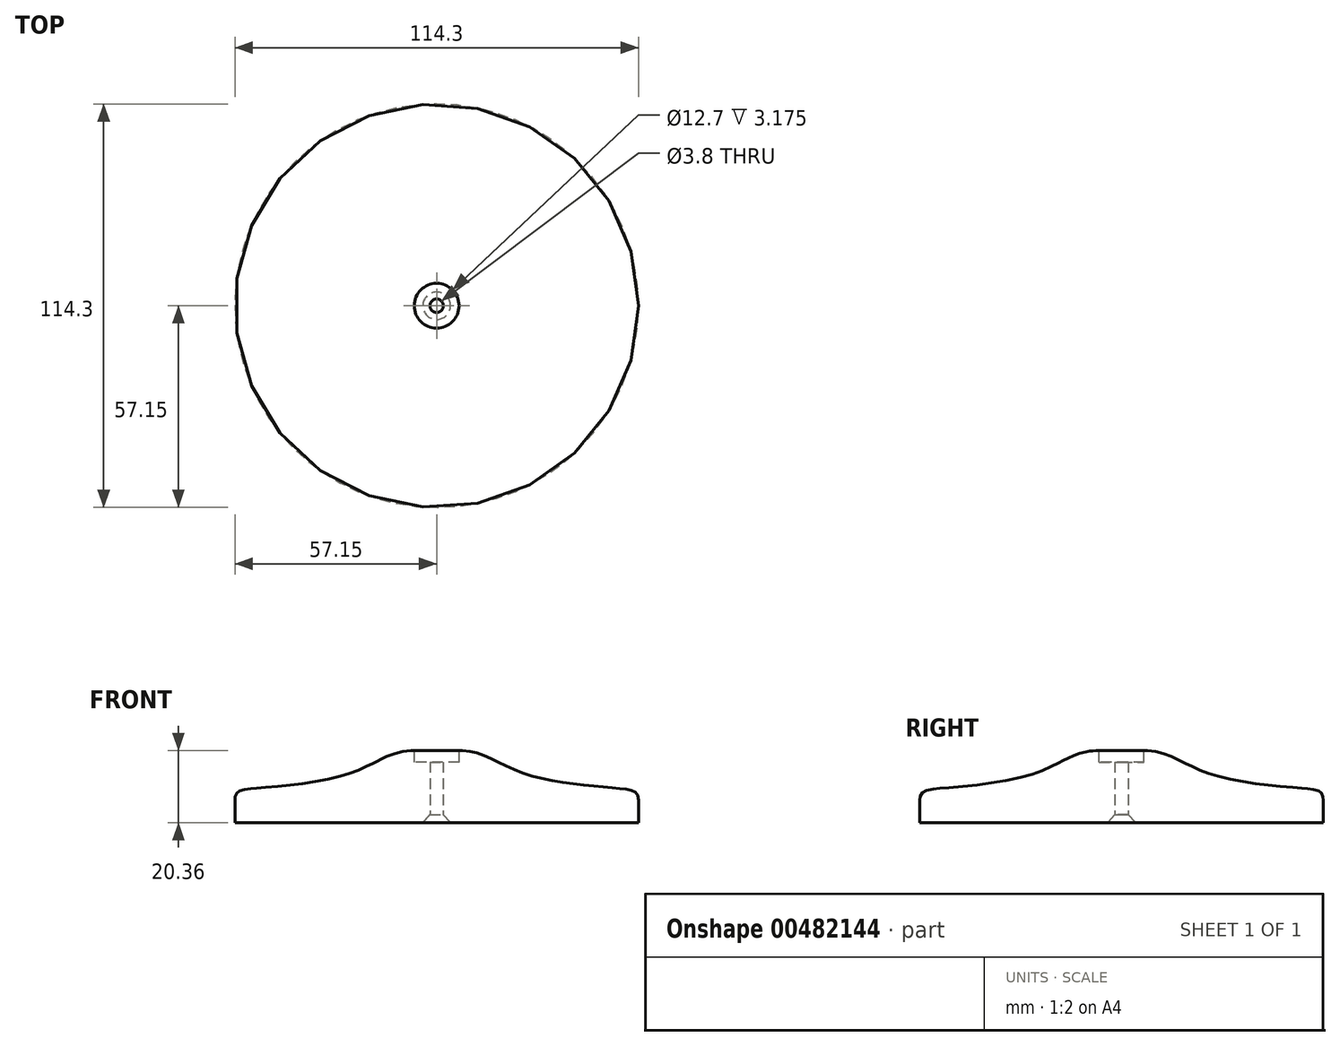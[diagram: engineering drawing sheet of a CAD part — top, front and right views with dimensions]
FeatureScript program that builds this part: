
annotation { "Feature Type Name" : "Feature", "Feature Type Description" : "" }
export const myFeature = defineFeature(function(context is Context, id is Id, definition is map)
    precondition{}
    {
        {
            var Q0;
            Q0=qCreatedBy(makeId("Top.planeOp"),FACE);
            var sketch = newSketch(context, id + "F0", { "sketchPlane" : qUnion([Q0])});
            skCircle(sketch, "E0", {"center": v(0, 0) * mm, "radius": 28.58 * mm, "construction": true});
            skSolve(sketch);
        }
        {
            var Q0;
            Q0=qCreatedBy(makeId("Front.planeOp"),FACE);
            var sketch = newSketch(context, id + "F1", { "sketchPlane" : qUnion([Q0])});
            skLineSegment(sketch, "E1", {"start": v(-57.15, 0) * mm, "end": v(0, 0) * mm});
            skLineSegment(sketch, "E2", {"start": v(-57.15, 0) * mm, "end": v(-57.15, 6.35) * mm});
            skFitSpline(sketch, "E3", {"points": [v(-57.15, 6.35) * mm, v(-52.75, 9.56) * mm, v(-24.5, 14) * mm, v(-6.35, 20.32) * mm], "startDerivative": vector(-0.27, 40.29) * mm, "endDerivative": vector(51.76, -3.83) * mm});
            skLineSegment(sketch, "E4", {"start": v(0, 0) * mm, "end": v(0, 17.15) * mm});
            skLineSegment(sketch, "E5", {"start": v(-6.35, 20.32) * mm, "end": v(-6.35, 17.15) * mm});
            skLineSegment(sketch, "E6", {"start": v(-6.35, 17.15) * mm, "end": v(0, 17.15) * mm});
            skLineSegment(sketch, "E7", {"start": v(0, 23.15) * mm, "end": v(0, -3.4) * mm, "construction": true});
            skSolve(sketch);
        }
        {
            var Q0;
            {var subQ1=sQuery(id+"F1.wireOp",EDGE,"E1");Q0=makeQuery(id+"F1.imprint","IMPRINT",FACE,{"disambiguationData":[TD([[makeQuery(id+"F1.imprint","IMPRINT",EDGE,{"derivedFrom":subQ1}),1.0]])]});}
            var Q1;
            Q1=sQuery(id+"F1.wireOp",EDGE,"E7");
            revolve(context, id + "F2", {"entities" : qUnion([Q0]), "axis" : qUnion([Q1]), "revolveType" : RevolveType.FULL});
        }
        {
            var Q0;
            Q0=sQuery(id+"F0.wireOp",VERTEX,"E0.center");
            var Q1;
            Q1=makeQuery(id+"F2.opRevolve","SWEPT_BODY",BODY,{"disambiguationData":[OSD([sQuery(id+"F1.wireOp",EDGE,"E1"),sQuery(id+"F1.wireOp",EDGE,"E2"),sQuery(id+"F1.wireOp",EDGE,"E3"),sQuery(id+"F1.wireOp",EDGE,"E4"),sQuery(id+"F1.wireOp",EDGE,"E5"),sQuery(id+"F1.wireOp",EDGE,"E6")])]});
            hole(context, id + "F3", {"style" : HoleStyle.C_SINK, "endStyle" : HoleEndStyle.THROUGH, "oppositeDirection" : true, "standardTappedOrClearance" : lookupTablePath({ "standard" : "ANSI", "fit" : "Normal (ASME)", "size" : "#6", "type" : "Clearance" }), "standardBlindInLast" : lookupTablePath({ "fit" : "Free", "standard" : "ANSI", "size" : "#6", "type" : "Clearance" }), "holeDiameter" : 3.8 * mm, "cSinkDiameter" : 7.8 * mm, "cSinkAngle" : 82 * degree, "isTappedThrough" : true, "tappedDepth" : 12.7 * mm, "tapClearance" : 3, "locations" : qUnion([Q0]), "scope" : qUnion([Q1])});
        }
    });
